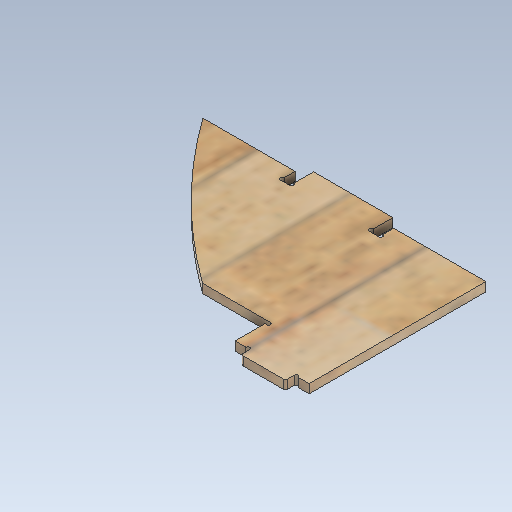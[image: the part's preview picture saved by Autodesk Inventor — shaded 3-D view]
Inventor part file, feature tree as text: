
AUTODESK INVENTOR PART (.ipt)
format: ipt  version: 2020 (Build 240168000, 168)  size: 243,712 bytes
history: native  units: mm
features: extrude x1, sketch x1
ambient origin geometry x8: Origin, YZ Plane, XZ Plane, XY Plane, X Axis, Y Axis, Z Axis, Center Point
bodies: Solid1 (feature_tree)
feature tree (2):
  extrude  "Extrusion1"  Depth=53.623333mm
  sketch  "Sketch1"  dims[d1=2.666667mm d2=30.0mm d4=2.666667mm d6=7.333333mm d7=7.333333mm d8=20.666667mm d9=2.666667mm d10=45.833333mm d11=119.5mm d12=62.333333mm d19=7.333333mm d41=6.0mm d42=0.0mm d53=2.666667mm d56=2.666667mm d58=6.5mm d59=13.333333mm d61=425.0mm d64=13.333333mm d67=7.333333mm d73=50.0mm d74=2.666667mm d75=6.0mm d76=191.29mm d77=6.5mm d78=6.5mm d79=6.5mm d80=1.333333mm d81=1.333333mm d82=90.0deg d83=2.666667mm d84=2.666667mm d85=2.666667mm d86=2.666667mm d87=53.623333mm]
